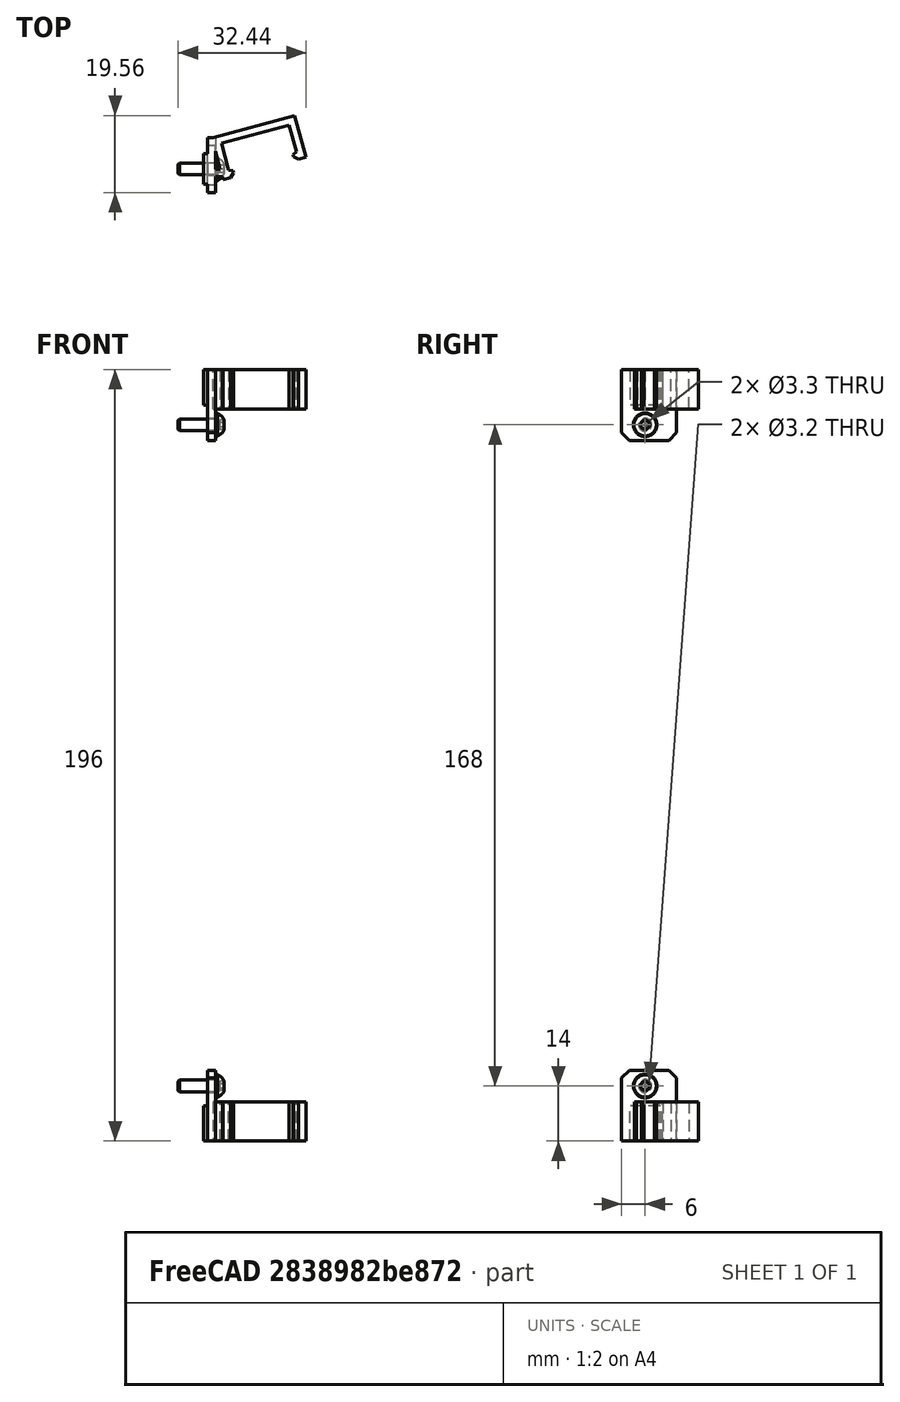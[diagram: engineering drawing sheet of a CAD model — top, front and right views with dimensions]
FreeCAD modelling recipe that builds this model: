
FCSTD DOCUMENT  (FreeCAD 0.19R24291 (Git))
Label: neo-pixel-assembly
License: Other
LicenseURL: GPL3
objects: Part::FeaturePython×4, PartDesign::CoordinateSystem×2, Part::Feature×2, App::Part×1, App::Link×1
note: 8 computed .brp shape members not serialized (recipe doc carries the construction recipe); baked Part::Feature solids carry a one-line shape summary decoded from their .brp
EXTERNAL_REF file=right-panel-assembly.FCStd obj=LCS_right_panel
EXTERNAL_REF file=right-panel-assembly.FCStd obj=Part005

FEATURE [Part::FeaturePython] Washer  label="M3-Washer"  # Fasteners workbench fastener (typed FeaturePython)
  Placement = pos=(2,0,32) rot=(0,1,0;1.5708rad)
  diameter = 4
  invert = true
  matchOuter = false
  offset = 0
  type = 5
FEATURE [Part::FeaturePython] Washer001  label="M3-Washer001"  # Fasteners workbench fastener (typed FeaturePython)
  Placement = pos=(2,0,-136) rot=(0,1,0;1.5708rad)
  diameter = 4
  invert = false
  matchOuter = false
  offset = 0
  type = 5
FEATURE [Part::FeaturePython] Screw  label="M3x10-Screw"  # Fasteners workbench fastener (typed FeaturePython)
  Placement = pos=(2.55,0,-136) rot=(0,1,0;1.5708rad)
  baseObject = -> Washer001 [Edge1]
  diameter = 1
  invert = false
  length = 2
  lengthCustom = 10
  matchOuter = false
  offset = 0
  thread = false
  type = 40
FEATURE [Part::FeaturePython] Screw001  label="M3x10-Screw001"  # Fasteners workbench fastener (typed FeaturePython)
  Placement = pos=(2.55,0,32) rot=(0,1,0;1.5708rad)
  baseObject = -> Washer [Edge1]
  diameter = 1
  invert = false
  length = 2
  lengthCustom = 10
  matchOuter = false
  offset = 0
  thread = false
  type = 40
FEATURE [PartDesign::CoordinateSystem] LCS_neopizel
  AttacherType = Attacher::AttachEngine3D
FEATURE [Part::Feature] Cut005001002  label="neo-pixel-arm"
  Placement = pos=(0,0,-150) rot=(0,0,1;0rad)
  shape: bbox 25.99 x 19.56 x 18 mm, 31 faces (baked)
FEATURE [Part::Feature] Part__Mirroring002  label="neo-pixel-arm-rev"
  Placement = pos=(-6e-15,0,46) rot=(0,1,0;3.14159rad)
  shape: bbox 25.99 x 19.56 x 18 mm, 31 faces (baked)
FEATURE [App::Part] Part  label="neo-pixel-mount"
  Group = -> [Washer,Washer001,Screw,Screw001,LCS_neopizel,Cut005001002,Part__Mirroring002]
  Origin = -> Origin
FEATURE [PartDesign::CoordinateSystem] LCS_Origin
  AttacherType = Attacher::AttachEngine3D
  MapMode = 2
  Support = -> [X_Axis001]
FEATURE [App::Link] right_panel  label="right-panel"
  AttachedBy = #LCS_right_panel
  AttachedTo = Parent Assembly#LCS_Origin
  AttachmentOffset = pos=(188,25,26) rot=(0,0,1;1.5708rad)
  LinkPlacement = pos=(188,25,26) rot=(0,0,1;1.5708rad)
  LinkedObject = -> <external right-panel-assembly.FCStd>#Part005
  Placement = pos=(188,25,26) rot=(0,0,1;1.5708rad)
  SolverId = Placement::ExpressionEngine
  expr: Placement = LCS_Origin.Placement * AttachmentOffset * right_panel_assembly#LCS_right_panel.Placement ^ -1

RESOLVED EXTERNAL PARTS (link-assembly join: the EXTERNAL_REF files above that resolve inside this repo's crawl, each included once):
---- part right-panel-assembly.FCStd = doc fcstd_e236a99d917d ----
FCSTD DOCUMENT  (FreeCAD 0.19R24291 (Git))
Label: right-panel-assembly
License: All rights reserved
LicenseURL: http://en.wikipedia.org/wiki/All_rights_reserved
objects: Part::Feature×24, App::Part×13, Part::FeaturePython×12, PartDesign::CoordinateSystem×1, Part::Box×1
note: 38 computed .brp shape members not serialized (recipe doc carries the construction recipe); baked Part::Feature solids carry a one-line shape summary decoded from their .brp

FEATURE [Part::Feature] Chamfer008001013  label="mounter-inner"
  shape: bbox 28 x 22 x 6 mm, 82 faces (baked)
FEATURE [Part::FeaturePython] Screw055  label="M6x16-Screw001"  # Fasteners workbench fastener (typed FeaturePython)
  Placement = pos=(15,0,7) rot=(0,0,1;0rad)
  baseObject = -> Chamfer008002001003 [Edge135]
  diameter = 4
  invert = false
  length = 3
  lengthCustom = 16
  matchOuter = false
  offset = 0
  thread = false
  type = 40
FEATURE [Part::Feature] Chamfer008002001009  label="mounter-inner004"
  shape: bbox 28 x 22 x 6 mm, 82 faces (baked)
FEATURE [Part::Feature] Chamfer008002001002  label="mounter-inner001"
  shape: bbox 28 x 22 x 6 mm, 82 faces (baked)
FEATURE [Part::Feature] Chamfer008002001004  label="mounter-inner002"
  shape: bbox 28 x 22 x 6 mm, 82 faces (baked)
FEATURE [Part::Feature] Chamfer008002001007  label="mounter-outer008"
  shape: bbox 17 x 28 x 11 mm, 53 faces (baked)
FEATURE [Part::Feature] Chamfer008002001016  label="mounter-inner008"
  shape: bbox 28 x 22 x 6 mm, 82 faces (baked)
FEATURE [Part::FeaturePython] Screw063  label="M6x16-Screw013"  # Fasteners workbench fastener (typed FeaturePython)
  Placement = pos=(15,0,7) rot=(0,0,1;0rad)
  baseObject = -> Chamfer008002001019 [Edge135]
  diameter = 4
  invert = false
  length = 3
  lengthCustom = 16
  matchOuter = false
  offset = 0
  thread = false
  type = 40
FEATURE [Part::Feature] Chamfer008002001022  label="mounter-inner011"
  shape: bbox 28 x 22 x 6 mm, 82 faces (baked)
FEATURE [Part::Feature] Chamfer008002001011  label="mounter-inner005"
  shape: bbox 28 x 22 x 6 mm, 82 faces (baked)
FEATURE [Part::FeaturePython] Screw057  label="M6x16-Screw003"  # Fasteners workbench fastener (typed FeaturePython)
  Placement = pos=(15,0,7) rot=(0,0,1;0rad)
  baseObject = -> Chamfer008002001007 [Edge135]
  diameter = 4
  invert = false
  length = 3
  lengthCustom = 16
  matchOuter = false
  offset = 0
  thread = false
  type = 40
FEATURE [Part::FeaturePython] Screw054  label="M6x16-Screw007"  # Fasteners workbench fastener (typed FeaturePython)
  Placement = pos=(15,0,7) rot=(0,0,1;0rad)
  baseObject = -> Chamfer008002001001 [Edge135]
  diameter = 4
  invert = false
  length = 3
  lengthCustom = 16
  matchOuter = false
  offset = 0
  thread = false
  type = 40
FEATURE [Part::Feature] Chamfer008002001012  label="mounter-outer005"
  shape: bbox 17 x 28 x 11 mm, 53 faces (baked)
FEATURE [Part::FeaturePython] Screw056  label="M6x16-Screw002"  # Fasteners workbench fastener (typed FeaturePython)
  Placement = pos=(15,0,7) rot=(0,0,1;0rad)
  baseObject = -> Chamfer008002001005 [Edge135]
  diameter = 4
  invert = false
  length = 3
  lengthCustom = 16
  matchOuter = false
  offset = 0
  thread = false
  type = 40
FEATURE [Part::Feature] Chamfer008002001020  label="mounter-outer001"
  shape: bbox 17 x 28 x 11 mm, 53 faces (baked)
FEATURE [Part::Feature] Chamfer008002001003  label="mounter-outer010"
  shape: bbox 17 x 28 x 11 mm, 53 faces (baked)
FEATURE [Part::FeaturePython] Screw062  label="M6x16-Screw012"  # Fasteners workbench fastener (typed FeaturePython)
  Placement = pos=(15,0,7) rot=(0,0,1;0rad)
  baseObject = -> Chamfer008002001017 [Edge135]
  diameter = 4
  invert = false
  length = 3
  lengthCustom = 16
  matchOuter = false
  offset = 0
  thread = false
  type = 40
FEATURE [Part::FeaturePython] Screw060  label="M6x16-Screw010"  # Fasteners workbench fastener (typed FeaturePython)
  Placement = pos=(15,0,7) rot=(0,0,1;0rad)
  baseObject = -> Chamfer008002001012 [Edge135]
  diameter = 4
  invert = false
  length = 3
  lengthCustom = 16
  matchOuter = false
  offset = 0
  thread = false
  type = 40
FEATURE [Part::Feature] Chamfer008002001013  label="mounter-inner006"
  shape: bbox 28 x 22 x 6 mm, 82 faces (baked)
FEATURE [Part::Feature] Chamfer008002001019  label="mounter-outer002"
  shape: bbox 17 x 28 x 11 mm, 53 faces (baked)
FEATURE [Part::Feature] Chamfer008002001006  label="mounter-inner003"
  shape: bbox 28 x 22 x 6 mm, 82 faces (baked)
FEATURE [App::Part] Part016  label="Panel-mounterr2-003"
  Group = -> [Chamfer008002001006,Chamfer008002001007,Screw057]
  Origin = -> Origin016
  Placement = pos=(315,3,39) rot=(-1,0,0;4.71239rad)
FEATURE [Part::FeaturePython] Screw064  label="M6x16-Screw014"  # Fasteners workbench fastener (typed FeaturePython)
  Placement = pos=(15,0,7) rot=(0,0,1;0rad)
  baseObject = -> Chamfer008002001020 [Edge135]
  diameter = 4
  invert = false
  length = 3
  lengthCustom = 16
  matchOuter = false
  offset = 0
  thread = false
  type = 40
FEATURE [PartDesign::CoordinateSystem] LCS_right_panel  label="LCS_right-panel"
  AttacherType = Attacher::AttachEngine3D
FEATURE [Part::Feature] Chamfer008002001023  label="mounter-outer"
  shape: bbox 17 x 28 x 11 mm, 53 faces (baked)
FEATURE [Part::Feature] Chamfer008002001018  label="mounter-inner009"
  shape: bbox 28 x 22 x 6 mm, 82 faces (baked)
FEATURE [App::Part] Part022  label="Panel-mounterr2-009"
  Group = -> [Chamfer008002001018,Chamfer008002001019,Screw063]
  Origin = -> Origin022
  Placement = pos=(39,3,445) rot=(-0.57735,0.57735,-0.57735;4.18879rad)
FEATURE [Part::Feature] Chamfer008002001001  label="mounter-outer011"
  shape: bbox 17 x 28 x 11 mm, 53 faces (baked)
FEATURE [App::Part] Part013  label="Panel-mounterr2-000"
  Group = -> [Chamfer008001013,Chamfer008002001001,Screw054]
  Origin = -> Origin013
  Placement = pos=(39,3,5) rot=(-0.57735,-0.57735,0.57735;4.18879rad)
FEATURE [Part::Feature] Chamfer008002001014  label="mounter-inner007"
  shape: bbox 28 x 22 x 6 mm, 82 faces (baked)
FEATURE [Part::Feature] Chamfer008002001008  label="mounter-outer007"
  shape: bbox 17 x 28 x 11 mm, 53 faces (baked)
FEATURE [Part::Feature] Chamfer008002001017  label="mounter-outer003"
  shape: bbox 17 x 28 x 11 mm, 53 faces (baked)
FEATURE [App::Part] Part021  label="Panel-mounterr2-008"
  Group = -> [Chamfer008002001016,Chamfer008002001017,Screw062]
  Origin = -> Origin021
  Placement = pos=(5,3,411) rot=(0,0.707107,-0.707107;3.14159rad)
FEATURE [Part::Box] Box002  label="panel-324x454x3mm"
  AttacherType = Attacher::AttachEngine3D
  Height = 454
  Length = 324
  Placement = pos=(-2,0,-2) rot=(0,0,1;0rad)
  Width = 3
FEATURE [Part::Feature] Chamfer008002001015  label="mounter-outer004"
  shape: bbox 17 x 28 x 11 mm, 53 faces (baked)
FEATURE [Part::Feature] Chamfer008002001010  label="mounter-outer006"
  shape: bbox 17 x 28 x 11 mm, 53 faces (baked)
FEATURE [App::Part] Part019  label="Panel-mounterr2-006"
  Group = -> [Chamfer008002001013,Chamfer008002001012,Screw060]
  Origin = -> Origin019
  Placement = pos=(281,3,445) rot=(-0.57735,0.57735,-0.57735;4.18879rad)
FEATURE [Part::FeaturePython] Screw065  label="M6x16-Screw015"  # Fasteners workbench fastener (typed FeaturePython)
  Placement = pos=(15,0,7) rot=(0,0,1;0rad)
  baseObject = -> Chamfer008002001023 [Edge135]
  diameter = 4
  invert = false
  length = 3
  lengthCustom = 16
  matchOuter = false
  offset = 0
  thread = false
  type = 40
FEATURE [Part::FeaturePython] Screw061  label="M6x16-Screw011"  # Fasteners workbench fastener (typed FeaturePython)
  Placement = pos=(15,0,7) rot=(0,0,1;0rad)
  baseObject = -> Chamfer008002001015 [Edge135]
  diameter = 4
  invert = false
  length = 3
  lengthCustom = 16
  matchOuter = false
  offset = 0
  thread = false
  type = 40
FEATURE [App::Part] Part020  label="Panel-mounterr2-007"
  Group = -> [Chamfer008002001014,Chamfer008002001015,Screw061]
  Origin = -> Origin020
  Placement = pos=(160,3,445) rot=(-0.57735,0.57735,-0.57735;4.18879rad)
FEATURE [Part::FeaturePython] Screw058  label="M6x16-Screw008"  # Fasteners workbench fastener (typed FeaturePython)
  Placement = pos=(15,0,7) rot=(0,0,1;0rad)
  baseObject = -> Chamfer008002001008 [Edge135]
  diameter = 4
  invert = false
  length = 3
  lengthCustom = 16
  matchOuter = false
  offset = 0
  thread = false
  type = 40
FEATURE [App::Part] Part017  label="Panel-mounterr2-004"
  Group = -> [Chamfer008002001009,Chamfer008002001008,Screw058]
  Origin = -> Origin017
  Placement = pos=(315,3,215) rot=(-1,0,0;4.71239rad)
FEATURE [App::Part] Part024  label="Panel-mounterr2-011"
  Group = -> [Chamfer008002001022,Chamfer008002001023,Screw065]
  Origin = -> Origin024
  Placement = pos=(5,3,39) rot=(0,0.707107,-0.707107;3.14159rad)
FEATURE [Part::Feature] Chamfer008002001005  label="mounter-outer009"
  shape: bbox 17 x 28 x 11 mm, 53 faces (baked)
FEATURE [App::Part] Part015  label="Panel-mounterr2-002"
  Group = -> [Chamfer008002001004,Chamfer008002001005,Screw056]
  Origin = -> Origin015
  Placement = pos=(280.5,3,5) rot=(-0.57735,-0.57735,0.57735;4.18879rad)
FEATURE [Part::Feature] Chamfer008002001021  label="mounter-inner010"
  shape: bbox 28 x 22 x 6 mm, 82 faces (baked)
FEATURE [App::Part] Part023  label="Panel-mounterr2-010"
  Group = -> [Chamfer008002001021,Chamfer008002001020,Screw064]
  Origin = -> Origin023
  Placement = pos=(5,3,215) rot=(0,0.707107,-0.707107;3.14159rad)
FEATURE [Part::FeaturePython] Screw059  label="M6x16-Screw009"  # Fasteners workbench fastener (typed FeaturePython)
  Placement = pos=(15,0,7) rot=(0,0,1;0rad)
  baseObject = -> Chamfer008002001010 [Edge135]
  diameter = 4
  invert = false
  length = 3
  lengthCustom = 16
  matchOuter = false
  offset = 0
  thread = false
  type = 40
FEATURE [App::Part] Part018  label="Panel-mounterr2-005"
  Group = -> [Chamfer008002001011,Chamfer008002001010,Screw059]
  Origin = -> Origin018
  Placement = pos=(315,3,411) rot=(-1,0,0;4.71239rad)
FEATURE [App::Part] Part014  label="Panel-mounterr2-001"
  Group = -> [Chamfer008002001002,Chamfer008002001003,Screw055]
  Origin = -> Origin014
  Placement = pos=(160,3,5) rot=(-0.57735,-0.57735,0.57735;4.18879rad)
FEATURE [App::Part] Part005  label="right-panel"
  Group = -> [Box002,Part013,Part014,Part015,Part016,Part017,Part018,Part019,Part020,Part021,Part022,Part023,Part024,LCS_right_panel]
  Origin = -> Origin005
